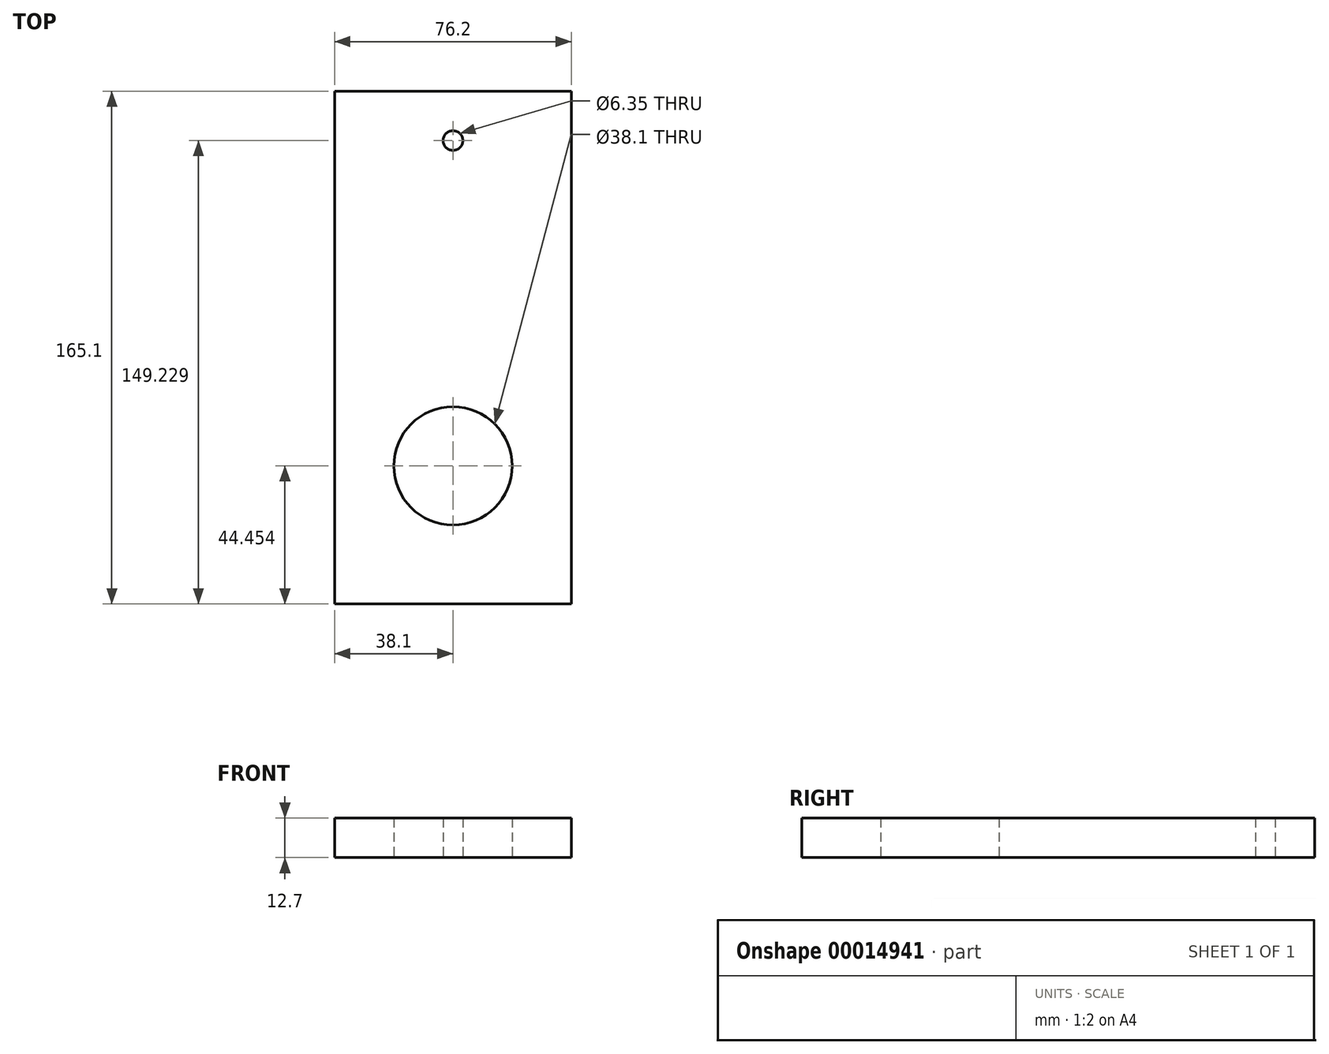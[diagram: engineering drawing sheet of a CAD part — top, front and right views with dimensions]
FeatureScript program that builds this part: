
annotation { "Feature Type Name" : "Feature", "Feature Type Description" : "" }
export const myFeature = defineFeature(function(context is Context, id is Id, definition is map)
    precondition{}
    {
        {
            var Q0;
            Q0=qCreatedBy(makeId("Top.planeOp"),FACE);
            var sketch = newSketch(context, id + "F0", { "sketchPlane" : qUnion([Q0])});
            skLineSegment(sketch, "E0.bottom", {"start": v(-114.7, -100.92) * mm, "end": v(-38.5, -100.92) * mm});
            skLineSegment(sketch, "E0.top", {"start": v(-114.7, 64.18) * mm, "end": v(-38.5, 64.18) * mm});
            skLineSegment(sketch, "E0.left", {"start": v(-114.7, -100.92) * mm, "end": v(-114.7, 64.18) * mm});
            skLineSegment(sketch, "E0.right", {"start": v(-38.5, -100.92) * mm, "end": v(-38.5, 64.18) * mm});
            skCircle(sketch, "E1", {"center": v(-76.6, 48.3) * mm, "radius": 3.18 * mm});
            skCircle(sketch, "E2", {"center": v(-76.6, -56.47) * mm, "radius": 19.05 * mm});
            skSolve(sketch);
        }
        {
            var Q0;
            Q0=makeQuery(id+"F0.imprint","IMPRINT",FACE,{"disambiguationData":[TD([[makeQuery(id+"F0.imprint","IMPRINT",EDGE,{"derivedFrom":sQuery(id+"F0.wireOp",EDGE,"E0.bottom")}),1.0]])]});
            extrude(context, id + "F1", {"entities" : qUnion([Q0]), "depth" : 12.7 * mm});
        }
    });
